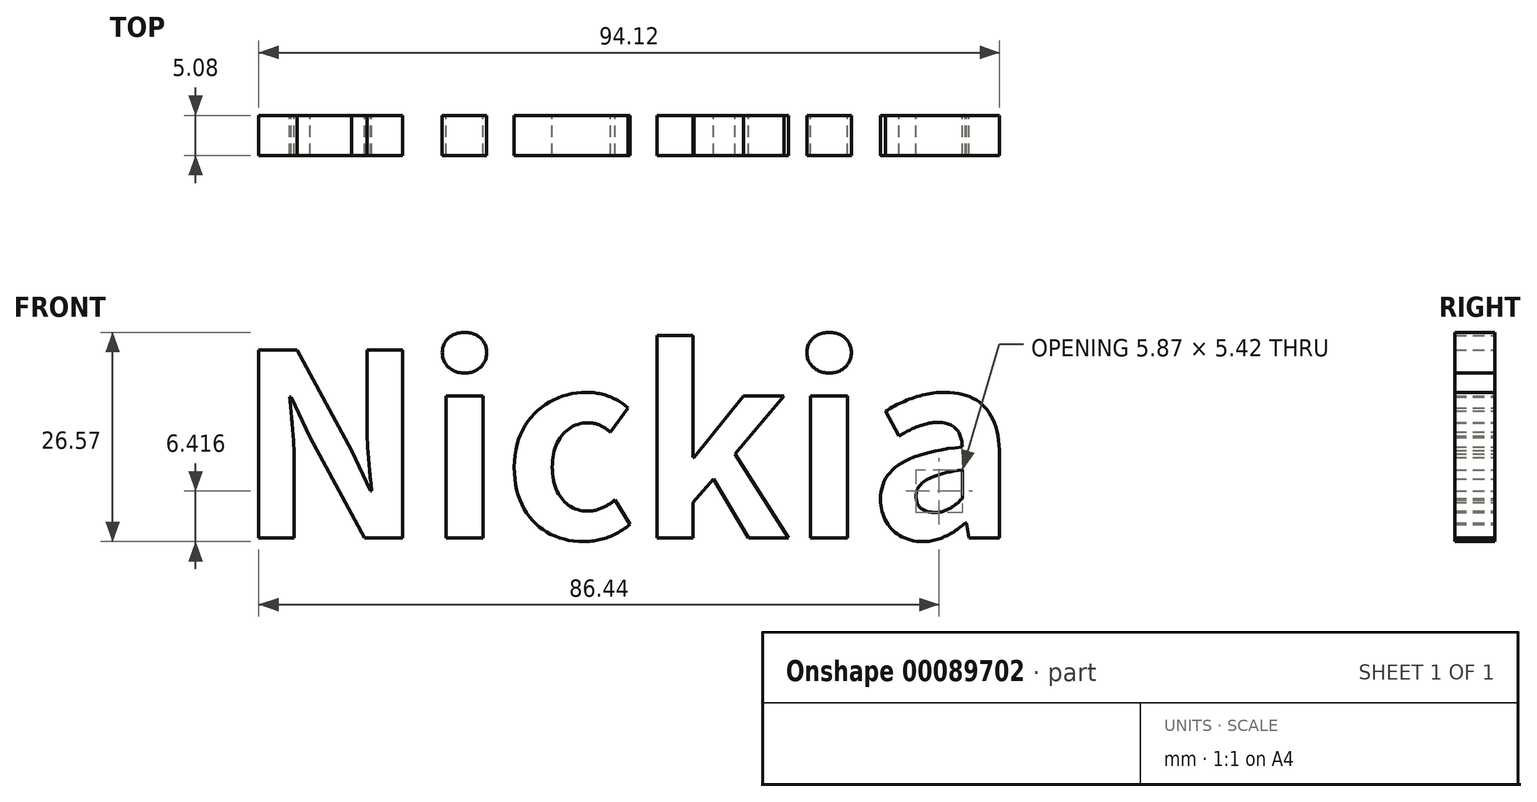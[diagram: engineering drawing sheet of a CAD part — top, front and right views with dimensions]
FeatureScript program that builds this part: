
annotation { "Feature Type Name" : "Feature", "Feature Type Description" : "" }
export const myFeature = defineFeature(function(context is Context, id is Id, definition is map)
    precondition{}
    {
        {
            var Q0;
            Q0=qCreatedBy(makeId("Front.planeOp"),FACE);
            var sketch = newSketch(context, id + "F0", { "sketchPlane" : qUnion([Q0])});
            skText(sketch, "E0", { "text": "Nickia", "fontName": "NotoSansCJKkr-Bold.otf"});
            const initialGuessF0  = {"E0": [-0.03772, 0, 1, 0, 0.02322]};
            skSetInitialGuess(sketch, initialGuessF0);
            skSolve(sketch);
        }
        {
            var Q0;
            Q0 = qSketchRegion(id + "F0", true);
            extrude(context, id + "F1", {"entities" : qUnion([Q0]), "depth" : 5.08 * mm});
        }
    });
